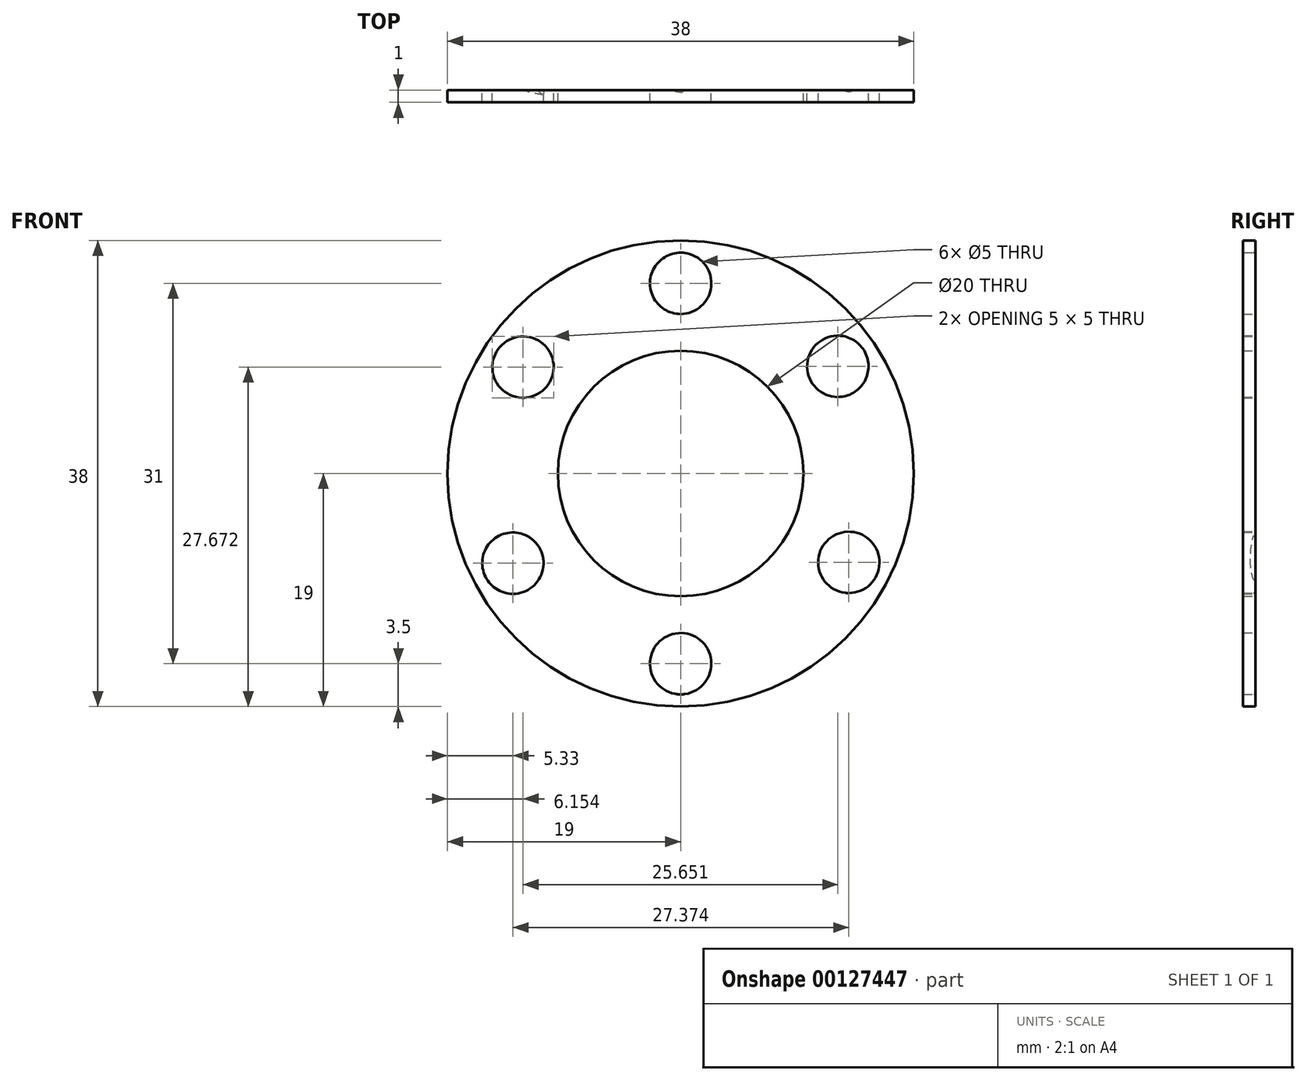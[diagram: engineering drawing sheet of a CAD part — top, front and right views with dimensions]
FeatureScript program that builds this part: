
annotation { "Feature Type Name" : "Feature", "Feature Type Description" : "" }
export const myFeature = defineFeature(function(context is Context, id is Id, definition is map)
    precondition{}
    {
        {
            var Q0;
            Q0=qCreatedBy(makeId("Front.planeOp"),FACE);
            var sketch = newSketch(context, id + "F0", { "sketchPlane" : qUnion([Q0])});
            skCircle(sketch, "E0", {"center": v(0, 0) * mm, "radius": 10 * mm});
            skCircle(sketch, "E1", {"center": v(0, 0) * mm, "radius": 19 * mm});
            skCircle(sketch, "E2", {"center": v(0, -15.5) * mm, "radius": 2.5 * mm});
            skCircle(sketch, "E3", {"center": v(-12.85, 8.67) * mm, "radius": 2.5 * mm});
            skCircle(sketch, "E4", {"center": v(12.8, 8.73) * mm, "radius": 2.5 * mm});
            skCircle(sketch, "E5", {"center": v(-13.67, -7.3) * mm, "radius": 2.5 * mm});
            skCircle(sketch, "E6", {"center": v(13.7, -7.24) * mm, "radius": 2.5 * mm});
            skCircle(sketch, "E7", {"center": v(0, 15.5) * mm, "radius": 2.5 * mm});
            skSolve(sketch);
        }
        {
            var Q0;
            Q0 = qSketchRegion(id + "F0", true);
            extrude(context, id + "F1", {"entities" : qUnion([Q0]), "depth" : 1 * mm});
        }
        {
            var Q0;
            Q0=qCreatedBy(makeId("Front.planeOp"),FACE);
            var sketch = newSketch(context, id + "F2", { "sketchPlane" : qUnion([Q0])});
            skLineSegment(sketch, "E8", {"start": v(-16.13, -7.29) * mm, "end": v(-11.13, -7.29) * mm});
            skArc(sketch, "E9", {"start": v(-16.13, -7.29) * mm, "mid": v(-13.63, -9.75) * mm, "end": v(-11.13, -7.29) * mm});
            skSolve(sketch);
        }
        {
            var Q0;
            Q0=makeQuery(id+"F2.imprint","IMPRINT",FACE,{"disambiguationData":[TD([[makeQuery(id+"F2.imprint","IMPRINT",EDGE,{"derivedFrom":sQuery(id+"F2.wireOp",EDGE,"E8")}),-1.0]])]});
            var Q1;
            Q1=sQuery(id+"F2.wireOp",EDGE,"E8");
            revolve(context, id + "F3", {"operationType" : NewBodyOperationType.ADD, "entities" : qUnion([Q0]), "axis" : qUnion([Q1]), "revolveType" : RevolveType.FULL});
        }
        {
            var Q0;
            Q0=qCreatedBy(makeId("Front.planeOp"),FACE);
            var sketch = newSketch(context, id + "F4", { "sketchPlane" : qUnion([Q0])});
            skLineSegment(sketch, "E10", {"start": v(0, 18) * mm, "end": v(0, 13) * mm});
            skArc(sketch, "E11", {"start": v(0, 13) * mm, "mid": v(2.47, 15.5) * mm, "end": v(0, 18) * mm});
            skLineSegment(sketch, "E12", {"start": v(0, -13) * mm, "end": v(0, -18) * mm});
            skLineSegment(sketch, "E13", {"start": v(-12.85, 11.17) * mm, "end": v(-12.85, 6.17) * mm});
            skLineSegment(sketch, "E14", {"start": v(12.8, 11.23) * mm, "end": v(12.8, 6.23) * mm});
            skLineSegment(sketch, "E15", {"start": v(13.7, -4.75) * mm, "end": v(13.7, -9.75) * mm});
            skArc(sketch, "E16", {"start": v(12.8, 6.23) * mm, "mid": v(15.27, 8.73) * mm, "end": v(12.8, 11.23) * mm});
            skArc(sketch, "E17", {"start": v(13.7, -9.75) * mm, "mid": v(16.13, -7.25) * mm, "end": v(13.7, -4.75) * mm});
            skArc(sketch, "E18", {"start": v(0, -18) * mm, "mid": v(2.47, -15.5) * mm, "end": v(0, -13) * mm});
            skArc(sketch, "E19", {"start": v(-12.85, 6.17) * mm, "mid": v(-10.4, 8.67) * mm, "end": v(-12.85, 11.17) * mm});
            skSolve(sketch);
        }
        {
            var Q0;
            Q0=makeQuery(id+"F4.imprint","IMPRINT",FACE,{"disambiguationData":[TD([[makeQuery(id+"F4.imprint","IMPRINT",EDGE,{"derivedFrom":sQuery(id+"F4.wireOp",EDGE,"E10")}),1.0]])]});
            var Q1;
            Q1=makeQuery(id+"F4.imprint","IMPRINT",FACE,{"disambiguationData":[TD([[makeQuery(id+"F4.imprint","IMPRINT",EDGE,{"derivedFrom":sQuery(id+"F4.wireOp",EDGE,"E12")}),1.0]])]});
            var Q2;
            Q2=sQuery(id+"F4.wireOp",EDGE,"E10");
            revolve(context, id + "F5", {"operationType" : NewBodyOperationType.ADD, "entities" : qUnion([Q0, Q1]), "axis" : qUnion([Q2]), "revolveType" : RevolveType.FULL});
        }
        {
            var Q0;
            Q0=makeQuery(id+"F4.imprint","IMPRINT",FACE,{"disambiguationData":[TD([[makeQuery(id+"F4.imprint","IMPRINT",EDGE,{"derivedFrom":sQuery(id+"F4.wireOp",EDGE,"E13")}),1.0]])]});
            var Q1;
            Q1=sQuery(id+"F4.wireOp",EDGE,"E13");
            revolve(context, id + "F6", {"operationType" : NewBodyOperationType.ADD, "entities" : qUnion([Q0]), "axis" : qUnion([Q1]), "revolveType" : RevolveType.FULL});
        }
        {
            var Q0;
            Q0=makeQuery(id+"F4.imprint","IMPRINT",FACE,{"disambiguationData":[TD([[makeQuery(id+"F4.imprint","IMPRINT",EDGE,{"derivedFrom":sQuery(id+"F4.wireOp",EDGE,"E14")}),1.0]])]});
            var Q1;
            Q1=sQuery(id+"F4.wireOp",EDGE,"E14");
            revolve(context, id + "F7", {"operationType" : NewBodyOperationType.ADD, "entities" : qUnion([Q0]), "axis" : qUnion([Q1]), "revolveType" : RevolveType.FULL});
        }
        {
            var Q0;
            Q0=makeQuery(id+"F4.imprint","IMPRINT",FACE,{"disambiguationData":[TD([[makeQuery(id+"F4.imprint","IMPRINT",EDGE,{"derivedFrom":sQuery(id+"F4.wireOp",EDGE,"E15")}),1.0]])]});
            var Q1;
            Q1=sQuery(id+"F4.wireOp",EDGE,"E15");
            revolve(context, id + "F8", {"operationType" : NewBodyOperationType.ADD, "entities" : qUnion([Q0]), "axis" : qUnion([Q1]), "revolveType" : RevolveType.FULL});
        }
    });
